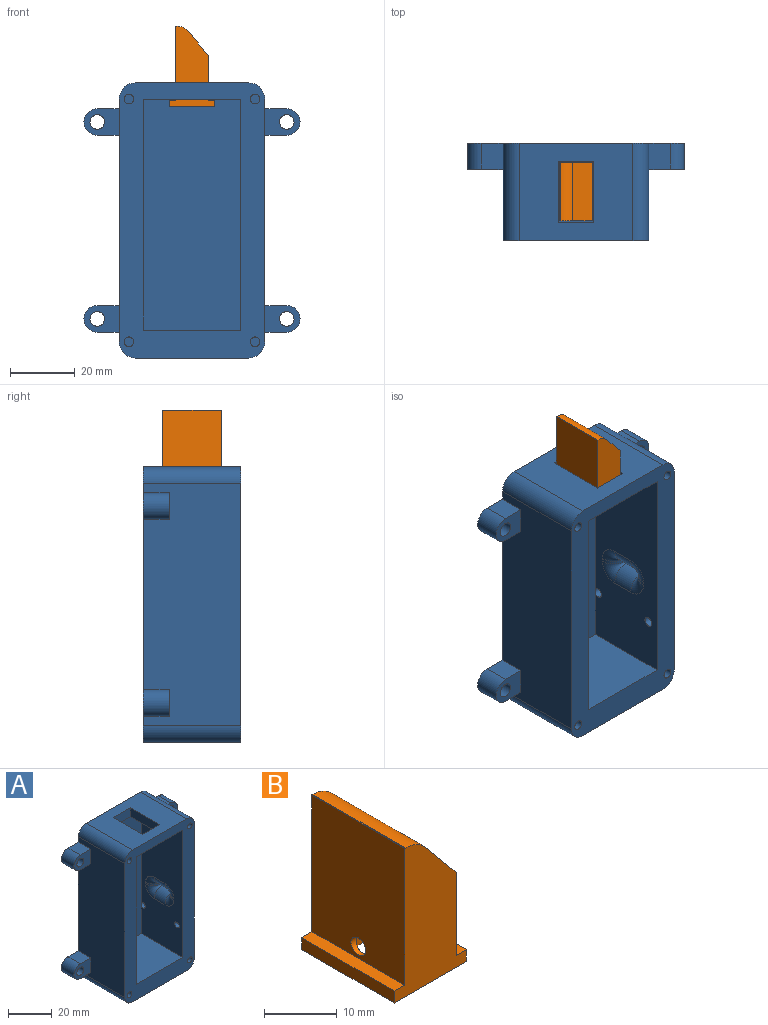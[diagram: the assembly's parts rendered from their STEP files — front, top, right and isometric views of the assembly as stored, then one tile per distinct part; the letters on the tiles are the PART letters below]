
ASSEMBLY  parts=2 mates=1
PART A: 74 faces, bbox 66.8x30x85 mm
  f0: plane 71.37x27mm, normal (-1,0,0), area 1723.1mm2, adj f3,f6,f8,f10,f43,f44,f45,f46
  f1: plane 75x30mm, normal (1,0,0), area 2037.4mm2, adj f8,f9,f23,f25,f27,f38,f40,f42
  f2: plane 75x30mm, normal (-1,0,0), area 2118.2mm2, adj f8,f9,f28,f29,f30,f33,f34,f35
  f3: plane 30x27mm, normal (0,0,-1), area 601mm2, adj f0,f5,f8,f10,f19,f20,f21,f22
  f4: plane 35x30mm, normal (0,0,1), area 841mm2, adj f8,f9,f19,f20,f21,f22,f70,f71
  f5: plane 71.37x27mm, normal (1,0,0), area 1926.9mm2, adj f3,f6,f8,f10
  f6: plane 30x27mm, normal (0,0,1), area 810mm2, adj f0,f5,f8,f10
  f7: plane 35x30mm, normal (0,0,-1), area 1050mm2, adj f8,f9,f72,f73
  f8: plane 85x45mm, normal (0,-1,0), area 1634.3mm2, adj f0,f1,f2,f3,f4,f5,f6,f7
  f9: plane 85x66.79mm, normal (0,1,0), area 4069.7mm2, adj f1,f2,f4,f7,f23,f24,f25,f26
  f10: plane 71.37x30mm, normal (0,-1,0), area 2141mm2, adj f0,f3,f5,f6,f60
  f11: plane 1x0.5mm, normal (0,-1,0), area 0.5mm2, adj f15,f16,f43,f54
  f12: plane 7x0.5mm, normal (0,0,1), area 3.5mm2, adj f15,f17,f47,f58
  f13: plane 7x0.5mm, normal (0,0,-1), area 3.5mm2, adj f16,f18,f46,f51
  f14: plane 1x0.5mm, normal (0,1,0), area 0.5mm2, adj f17,f18,f50,f55
  f15: cylinder r=0.5mm len=0.5mm, axis (1,0,0), area 0.4mm2, adj f11,f12,f45,f56
  f16: cylinder r=0.5mm len=0.5mm, axis (-1,0,0), area 0.4mm2, adj f11,f13,f44,f52
  f17: cylinder r=0.5mm len=0.5mm, axis (-1,0,0), area 0.4mm2, adj f12,f14,f49,f57
  f18: cylinder r=0.5mm len=0.5mm, axis (1,0,0), area 0.4mm2, adj f13,f14,f48,f53
  f19: plane 11x5mm, normal (0,-1,0), area 55mm2, adj f3,f4,f20,f22
  f20: plane 19x5mm, normal (1,0,0), area 95mm2, adj f3,f4,f19,f21
  f21: plane 11x5mm, normal (0,1,0), area 55mm2, adj f3,f4,f20,f22
  f22: plane 19x5mm, normal (-1,0,0), area 95mm2, adj f3,f4,f19,f21
  f23: plane 8x6.77mm, normal (0,0,1), area 54.2mm2, adj f1,f9,f24,f27
  f24: cylinder r=4.12mm len=8.24mm, axis (0,1,0), area 103.5mm2, adj f9,f23,f25,f27
  f25: plane 8x6.77mm, normal (0,0,-1), area 54.2mm2, adj f1,f9,f24,f27
  f26: cylinder r=2.25mm len=8mm, axis (0,1,0), area 113.1mm2, adj f9,f27
  f27: plane 10.89x8.24mm, normal (0,-1,0), area 66.5mm2, adj f1,f23,f24,f25,f26
  f28: plane 8x6.77mm, normal (0,0,-1), area 54.2mm2, adj f2,f9,f30,f31
  f29: plane 8x6.77mm, normal (0,0,1), area 54.2mm2, adj f2,f9,f30,f31
  f30: plane 10.89x8.24mm, normal (0,-1,0), area 66.5mm2, adj f2,f28,f29,f31,f32
  f31: cylinder r=4.12mm len=8.24mm, axis (0,1,0), area 103.5mm2, adj f9,f28,f29,f30
  f32: cylinder r=2.25mm len=8mm, axis (0,1,0), area 113.1mm2, adj f9,f30
  f33: plane 10.89x8.24mm, normal (0,-1,0), area 66.5mm2, adj f2,f34,f35,f36,f37
  f34: plane 8x6.77mm, normal (0,0,1), area 54.2mm2, adj f2,f9,f33,f37
  f35: plane 8x6.77mm, normal (0,0,-1), area 54.2mm2, adj f2,f9,f33,f37
  f36: cylinder r=2.25mm len=8mm, axis (0,1,0), area 113.1mm2, adj f9,f33
  f37: cylinder r=4.12mm len=8.24mm, axis (0,1,0), area 103.5mm2, adj f9,f33,f34,f35
  f38: plane 8x6.77mm, normal (0,0,1), area 54.2mm2, adj f1,f9,f39,f42
  f39: cylinder r=4.12mm len=8.24mm, axis (0,1,0), area 103.5mm2, adj f9,f38,f40,f42
  f40: plane 8x6.77mm, normal (0,0,-1), area 54.2mm2, adj f1,f9,f39,f42
  f41: cylinder r=2.25mm len=8mm, axis (0,1,0), area 113.1mm2, adj f9,f42
  f42: plane 10.89x8.24mm, normal (0,-1,0), area 66.5mm2, adj f1,f38,f39,f40,f41
  f43: cylinder r=5mm len=5mm, axis (0,0,-1), area 7.9mm2, adj f0,f11,f44,f45
  f44: torus R=5.5mm, axis (1,0,0), area 28.6mm2, adj f0,f16,f43,f46
  f45: torus R=5.5mm, axis (1,0,0), area 28.6mm2, adj f0,f15,f43,f47
  f46: cylinder r=5mm len=7mm, axis (0,1,0), area 55mm2, adj f0,f13,f44,f48
  f47: cylinder r=5mm len=7mm, axis (0,-1,0), area 55mm2, adj f0,f12,f45,f49
  f48: torus R=5.5mm, axis (1,0,0), area 28.6mm2, adj f0,f18,f46,f50
  f49: torus R=5.5mm, axis (1,0,0), area 28.6mm2, adj f0,f17,f47,f50
  f50: cylinder r=5mm len=5mm, axis (0,0,1), area 7.9mm2, adj f0,f14,f48,f49
  f51: cylinder r=2mm len=7mm, axis (0,1,0), area 22mm2, adj f1,f13,f52,f53
  f52: torus R=2.5mm, axis (1,0,0), area 6.1mm2, adj f1,f16,f51,f54
  f53: torus R=2.5mm, axis (1,0,0), area 6.1mm2, adj f1,f18,f51,f55
  f54: cylinder r=2mm len=2mm, axis (0,0,-1), area 3.1mm2, adj f1,f11,f52,f56
  f55: cylinder r=2mm len=2mm, axis (0,0,1), area 3.1mm2, adj f1,f14,f53,f57
  f56: torus R=2.5mm, axis (1,0,0), area 6.1mm2, adj f1,f15,f54,f58
  f57: torus R=2.5mm, axis (1,0,0), area 6.1mm2, adj f1,f17,f55,f58
  f58: cylinder r=2mm len=7mm, axis (0,-1,0), area 22mm2, adj f1,f12,f56,f57
  f59: cylinder r=1.5mm len=7.5mm, axis (1,0,0), area 70.7mm2, adj f0,f1
  f60: plane 1.89x0.34mm, normal (1,0,0), area 0.4mm2, adj f10,f61
  f61: cylinder r=1.5mm len=7.5mm, axis (1,0,0), area 70.7mm2, adj f0,f1,f60
  f62: cylinder r=1.5mm len=25mm, axis (0,-1,0), area 235.6mm2, adj f8,f63
  f63: plane 3x3mm, normal (0,-1,0), area 7.1mm2, adj f62
  f64: cylinder r=1.5mm len=25mm, axis (0,-1,0), area 235.6mm2, adj f8,f65
  f65: plane 3x3mm, normal (0,-1,0), area 7.1mm2, adj f64
  f66: cylinder r=1.5mm len=25mm, axis (0,-1,0), area 235.6mm2, adj f8,f67
  f67: plane 3x3mm, normal (0,-1,0), area 7.1mm2, adj f66
  f68: cylinder r=1.5mm len=25mm, axis (0,-1,0), area 235.6mm2, adj f8,f69
  f69: plane 3x3mm, normal (0,-1,0), area 7.1mm2, adj f68
  f70: cylinder r=5mm len=30mm, axis (0,-1,0), area 235.6mm2, adj f1,f4,f8,f9
  f71: cylinder r=5mm len=30mm, axis (0,1,0), area 235.6mm2, adj f2,f4,f8,f9
  f72: cylinder r=5mm len=30mm, axis (0,-1,0), area 235.6mm2, adj f2,f7,f8,f9
  f73: cylinder r=5mm len=30mm, axis (0,1,0), area 235.6mm2, adj f1,f7,f8,f9
PART B: 16 faces, bbox 14x18x25 mm
  f0: plane 18x2mm, normal (-1,0,0), area 36mm2, adj f2,f3,f12,f13
  f1: plane 18x2mm, normal (1,0,0), area 36mm2, adj f3,f6,f12,f13
  f2: plane 18x2mm, normal (0,0,1), area 36mm2, adj f0,f11,f12,f13
  f3: plane 18x14mm, normal (0,0,-1), area 195.3mm2, adj f0,f1,f4,f12,f13
  f4: cylinder r=4.25mm len=12mm, axis (0,0,-1), area 306.1mm2, adj f3,f5,f14,f15
  f5: plane 8.5x8.5mm, normal (0,0,-1), area 56.7mm2, adj f4
  f6: plane 18x2mm, normal (0,0,1), area 36mm2, adj f1,f10,f12,f13
  f7: cylinder r=5mm len=18mm, axis (0,-1,0), area 78.8mm2, adj f8,f9,f12,f13
  f8: plane 18x7.22mm, normal (0.77,0,0.64), area 169.1mm2, adj f7,f10,f12,f13
  f9: plane 18x0.14mm, normal (0,0,1), area 2.6mm2, adj f7,f11,f12,f13
  f10: plane 18x13.99mm, normal (1,0,0), area 244.1mm2, adj f6,f8,f12,f13,f14
  f11: plane 23x18mm, normal (-1,0,0), area 407.6mm2, adj f2,f9,f12,f13,f15
  f12: plane 25x14mm, normal (0,1,0), area 223.4mm2, adj f0,f1,f2,f3,f6,f7,f8,f9
  f13: plane 25x14mm, normal (0,-1,0), area 223.4mm2, adj f0,f1,f2,f3,f6,f7,f8,f9
  f14: cylinder r=1.56mm len=3.13mm, axis (1,0,0), area 8.8mm2, adj f4,f10
  f15: cylinder r=1.43mm len=2.85mm, axis (-1,0,0), area 7.8mm2, adj f4,f11
PLACE A t=(-5.07,4.73,26.65)mm fixed
PLACE B t=(-5.07,4.73,27.2)mm
MATE slider A.f4 <-> B.f4  axis (0,0,1) through (-5.07,4.73,34.6)mm
